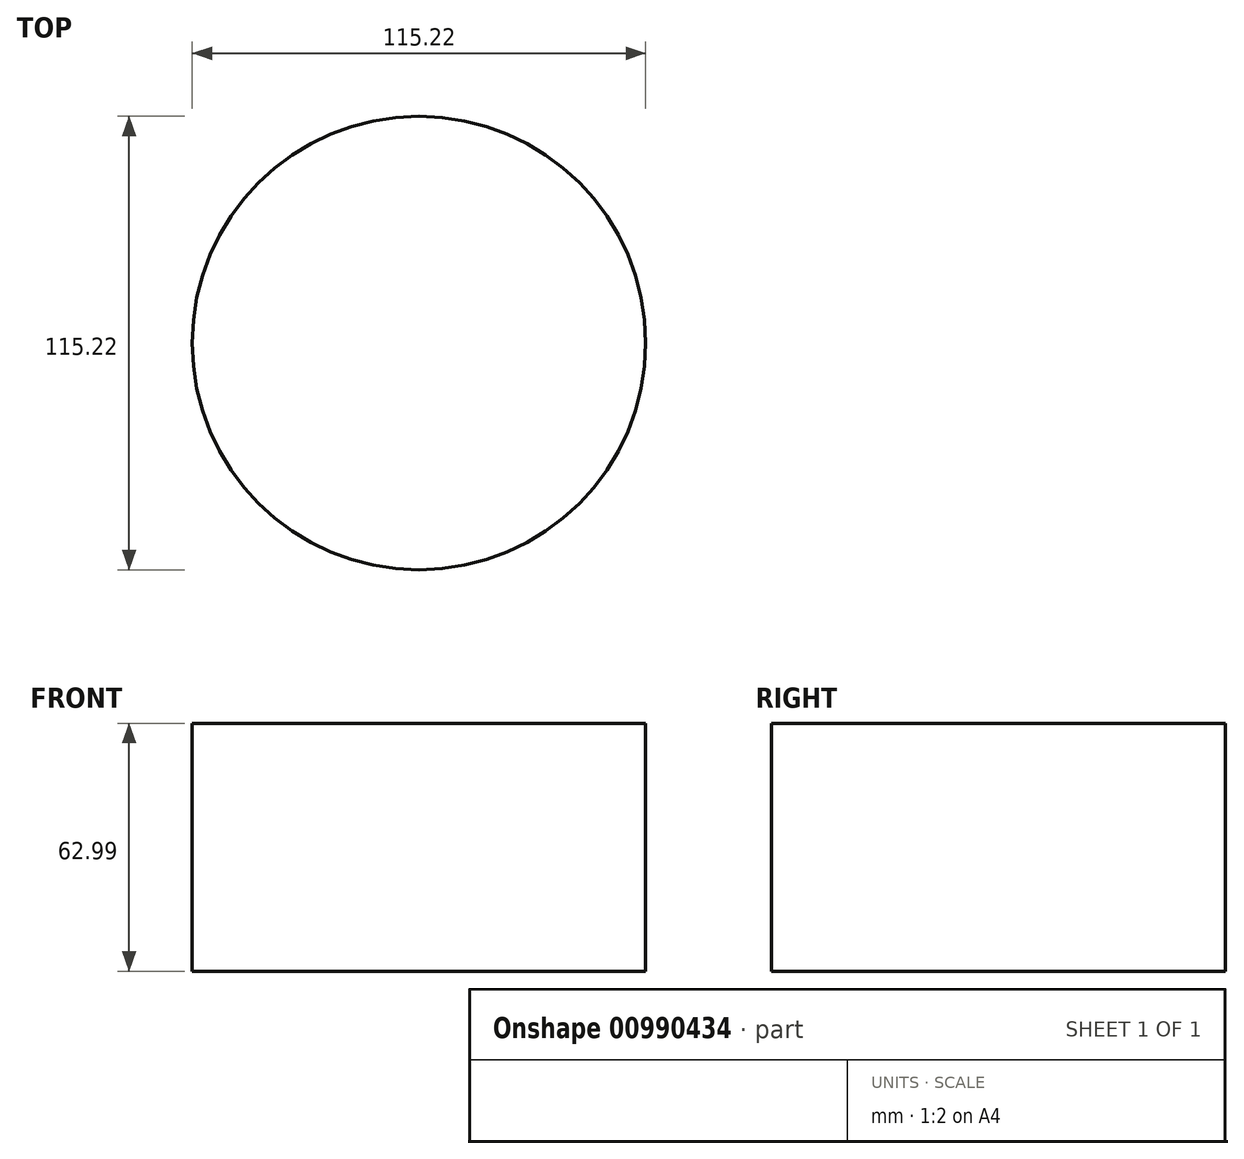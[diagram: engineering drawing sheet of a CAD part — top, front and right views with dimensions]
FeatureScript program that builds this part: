
annotation { "Feature Type Name" : "Feature", "Feature Type Description" : "" }
export const myFeature = defineFeature(function(context is Context, id is Id, definition is map)
    precondition{}
    {
        {
            var Q0;
            Q0=qCreatedBy(makeId("Top.planeOp"),FACE);
            var sketch = newSketch(context, id + "F0", { "sketchPlane" : qUnion([Q0])});
            skCircle(sketch, "E0", {"center": v(0, 0) * mm, "radius": 57.61 * mm});
            skSolve(sketch);
        }
        {
            var Q0;
            Q0=makeQuery(id+"F0.imprint","IMPRINT",FACE,{"disambiguationData":[TD([[makeQuery(id+"F0.imprint","IMPRINT",EDGE,{"derivedFrom":sQuery(id+"F0.wireOp",EDGE,"E0")}),1.0]])]});
            extrude(context, id + "F1", {"entities" : qUnion([Q0]), "depth" : 63 * mm, "offsetDistance" : 25.4 * mm});
        }
    });
